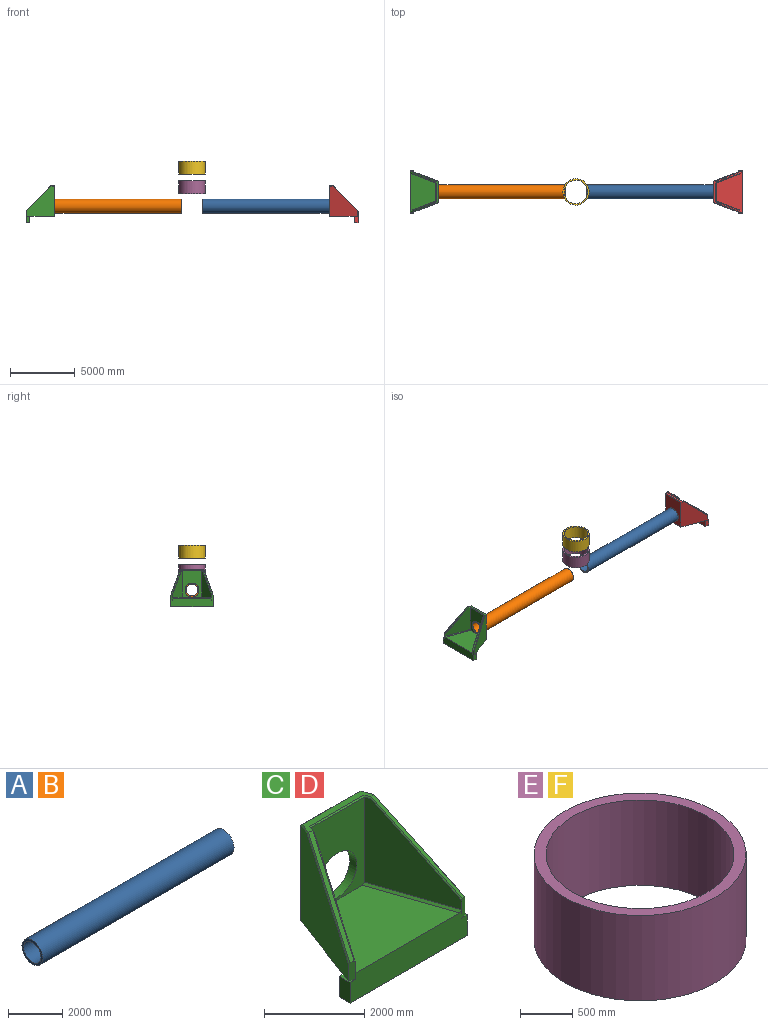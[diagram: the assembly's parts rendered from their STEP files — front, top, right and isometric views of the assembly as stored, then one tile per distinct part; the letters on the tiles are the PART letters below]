
ASSEMBLY  parts=6 mates=6
PART A: 4 faces, bbox 10000x1080x1080 mm
  f0: cylinder r=450mm len=10000mm, axis (-1,0,0), area 28274333.9mm2, adj f2,f3
  f1: cylinder r=540mm len=10000mm, axis (-1,0,0), area 33929200.7mm2, adj f2,f3
  f2: plane 1080x1080mm, normal (1,0,0), area 279915.9mm2, adj f0,f1
  f3: plane 1080x1080mm, normal (-1,0,0), area 279915.9mm2, adj f0,f1
PART B: same geometry as A
PART C: 33 faces, bbox 3300x2200x2850 mm
  f0: plane 3090.14x1900mm, normal (0,0,-1), area 4522935.6mm2, adj f1,f3,f16,f26
  f1: plane 2325x2147.52mm, normal (0.94,0.35,0), area 3425055.3mm2, adj f0,f3,f5,f8,f9,f24
  f2: plane 2124.99x2000mm, normal (-0.94,-0.35,0), area 2578544.8mm2, adj f4,f5,f11,f12,f31
  f3: plane 2325x1670.84mm, normal (0,1,0), area 2968620.2mm2, adj f0,f1,f10,f16,f30
  f4: plane 2125x1500mm, normal (0,-1,0), area 2268742.3mm2, adj f2,f13,f15,f17,f30,f31,f32
  f5: plane 450x140.52mm, normal (0.35,-0.94,0), area 66634.8mm2, adj f1,f2,f7,f8,f11,f14,f24
  f6: plane 1839.17x306.77mm, normal (0,0,1), area 283560.2mm2, adj f7,f9,f10,f12,f13,f19,f21,f23
  f7: plane 1900x1894.47mm, normal (0.24,-0.65,0.72), area 274773.1mm2, adj f5,f6,f8,f11
  f8: plane 1934.61x1877.63mm, normal (0.83,-0.21,0.51), area 97392.6mm2, adj f1,f5,f7,f9
  f9: plane 296.78x121.42mm, normal (0.66,0.25,0.71), area 10386.6mm2, adj f1,f6,f8,f10
  f10: plane 1670.84x25mm, normal (0,0.71,0.71), area 58459.8mm2, adj f3,f6,f9,f21
  f11: plane 1934.61x1868.88mm, normal (-0.49,-0.71,0.51), area 97392.6mm2, adj f2,f5,f7,f12
  f12: plane 156.77x75.9mm, normal (-0.66,-0.25,0.71), area 5432.6mm2, adj f2,f6,f11,f13
  f13: plane 1534.7x25mm, normal (0,-0.71,0.71), area 53646.4mm2, adj f4,f6,f12,f23
  f14: plane 3300x700.01mm, normal (0,-1,0), area 2101769.3mm2, adj f5,f15,f18,f24,f25,f27,f28,f29
  f15: plane 2887.26x2000mm, normal (0,-0.02,1), area 4281850.7mm2, adj f4,f14,f31,f32
  f16: plane 2325x2147.52mm, normal (-0.94,0.35,0), area 3425055.3mm2, adj f0,f3,f18,f20,f21,f29
  f17: plane 2124.99x2000mm, normal (0.94,-0.35,0), area 2578544.8mm2, adj f4,f18,f22,f23,f32
  f18: plane 450x140.52mm, normal (-0.35,-0.94,0), area 66634.8mm2, adj f14,f16,f17,f19,f20,f22,f29
  f19: plane 1900x1894.47mm, normal (-0.24,-0.65,0.72), area 274773.1mm2, adj f6,f18,f20,f22
  f20: plane 1934.61x1877.63mm, normal (-0.83,-0.21,0.51), area 97392.6mm2, adj f16,f18,f19,f21
  f21: plane 296.78x121.42mm, normal (-0.66,0.25,0.71), area 10386.6mm2, adj f6,f10,f16,f20
  f22: plane 1934.61x1868.88mm, normal (0.49,-0.71,0.51), area 97392.6mm2, adj f17,f18,f19,f23
  f23: plane 156.77x75.9mm, normal (0.66,-0.25,0.71), area 5432.6mm2, adj f6,f13,f17,f22
  f24: plane 300x153mm, normal (0,0,1), area 18873mm2, adj f1,f5,f14,f25,f26
  f25: plane 500x300mm, normal (1,0,0), area 150000mm2, adj f14,f24,f26,f28
  f26: plane 3300x500mm, normal (0,1,0), area 1650000mm2, adj f0,f24,f25,f27,f28,f29
  f27: plane 500x300mm, normal (-1,0,0), area 150000mm2, adj f14,f26,f28,f29
  f28: plane 3300x300mm, normal (0,0,-1), area 990000mm2, adj f14,f25,f26,f27
  f29: plane 300x153mm, normal (0,0,1), area 18873mm2, adj f14,f16,f18,f26,f27
  f30: cylinder r=540mm len=1080mm, axis (0,1,0), area 678584mm2, adj f3,f4
  f31: plane 2000x800.37mm, normal (-0.66,-0.26,0.7), area 151663.9mm2, adj f2,f4,f14,f15
  f32: plane 2000x800.37mm, normal (0.66,-0.26,0.7), area 151663.9mm2, adj f4,f14,f15,f17
PART D: same geometry as C
PART E: 4 faces, bbox 2030x2030x1000 mm
  f0: cylinder r=900mm len=1800mm, axis (0,0,-1), area 5654866.8mm2, adj f2,f3
  f1: cylinder r=1015mm len=2030mm, axis (0,0,-1), area 6377433.1mm2, adj f2,f3
  f2: plane 2030x2030mm, normal (0,0,1), area 691857.2mm2, adj f0,f1
  f3: plane 2030x2030mm, normal (0,0,-1), area 691857.2mm2, adj f0,f1
PART F: same geometry as E
PLACE A rot(axis=(-1,0,0),0deg) t=(800,0,958.9)mm
PLACE B rot(axis=(1,0,0),0deg) t=(-10800,0,958.9)mm
PLACE C rot(axis=(0,0,-1),90deg) t=(-12800,0,168.9)mm
PLACE D rot(axis=(0,0,1),90deg) t=(12800,0,168.9)mm
PLACE E t=(0,0,1919.92)mm
PLACE F t=(0,0,3432.54)mm
MATE slider E.f0 <-> F.f1  axis (0,0,-1) through (0,0,2919.92)mm
MATE slider B.f0 <-> A.f1  axis (1,0,0) through (-800,0,958.9)mm
MATE fastened A.f1 <-> D.f30  axis (1,0,0) through (10800,0,958.9)mm
MATE slider B.f0 <-> C.f30  axis (-1,0,0) through (-10800,0,958.9)mm
MATE fastened B.f1 <-> C.f30  axis (-1,0,0) through (-10800,0,958.9)mm
MATE slider A.f1 <-> D.f30  axis (-1,0,0) through (5800,0,958.9)mm
